FCSTD DOCUMENT  (FreeCAD 0.18R13588 (Git))
Label: footprint-template-roundrect-polylines
License: All rights reserved
LicenseURL: http://en.wikipedia.org/wiki/All_rights_reserved
objects: Sketcher::SketchObject×3, App::Annotation×2, App::DocumentObjectGroup×1
note: 3 computed .brp shape members not serialized (recipe doc carries the construction recipe); baked Part::Feature solids carry a one-line shape summary decoded from their .brp

FEATURE [App::Annotation] Text  label="Ref#_1.0mm"
  LabelText = REF**
  Position = (-30,-16,0)
FEATURE [App::Annotation] Text001  label="Value#_1.0mm"
  LabelText = Value 
  Position = (-30,-20,0)
FEATURE [Sketcher::SketchObject] Sketch003  label="F_Silks_0.16"
  sketch-geometry (4):
    g0: LineSegment StartX=-36 StartY=14 StartZ=0 EndX=24 EndY=14 EndZ=0
    g1: LineSegment StartX=24 StartY=14 StartZ=0 EndX=24 EndY=-26 EndZ=0
    g2: LineSegment StartX=24 StartY=-26 StartZ=0 EndX=-36 EndY=-26 EndZ=0
    g3: LineSegment StartX=-36 StartY=-26 StartZ=0 EndX=-36 EndY=14 EndZ=0
  constraints (12):
    c: Coincident(g0,g1)
    c: Coincident(g1,g2)
    c: Coincident(g2,g3)
    c: Coincident(g3,g0)
    c: Horizontal(g0)
    c: Horizontal(g2)
    c: Vertical(g1)
    c: Vertical(g3)
    c: DistanceY(g3,g3) = 40
    c: DistanceX(g0,g0) = 60
    c: DistanceY(g-1,g0) = 14
    c: DistanceX(g0,g-1) = 36
FEATURE [Sketcher::SketchObject] Sketch007  label="Pads_Poly"
  sketch-geometry (10):
    g0: LineSegment StartX=-20 StartY=-6 StartZ=0 EndX=-14 EndY=-1 EndZ=0
    g1: LineSegment StartX=-14 StartY=-1 StartZ=0 EndX=-10 EndY=12 EndZ=0
    g2: LineSegment StartX=-10 StartY=12 StartZ=0 EndX=21 EndY=-8 EndZ=0
    g3: LineSegment StartX=21 StartY=-8 StartZ=0 EndX=-20 EndY=-6 EndZ=0
    g4: Circle CenterX=0 CenterY=0 CenterZ=0 NormalX=0 NormalY=0 NormalZ=1 AngleXU=0 Radius=1.5
    g5: LineSegment StartX=-25 StartY=-18 StartZ=0 EndX=-21 EndY=-12 EndZ=0
    g6: LineSegment StartX=-21 StartY=-12 StartZ=0 EndX=-9 EndY=-16 EndZ=0
    g7: LineSegment StartX=-9 StartY=-16 StartZ=0 EndX=-21 EndY=-22 EndZ=0
    g8: LineSegment StartX=-21 StartY=-22 StartZ=0 EndX=-25 EndY=-18 EndZ=0
    g9: Circle CenterX=-19 CenterY=-16.5 CenterZ=0 NormalX=0 NormalY=0 NormalZ=1 AngleXU=0 Radius=1.24416
  constraints (28):
    c: Coincident(g0,g1)
    c: Coincident(g1,g2)
    c: Coincident(g2,g3)
    c: Coincident(g3,g0)
    c: DistanceX(g0,g-1) = 14
    c: DistanceY(g0,g-1) = 1
    c: DistanceX(g0,g-1) = 20
    c: DistanceY(g0,g-1) = 6
    c: DistanceX(g-1,g2) = 21
    c: DistanceY(g2,g-1) = 8
    c: DistanceX(g1,g-1) = 10
    c: DistanceY(g-1,g1) = 12
    c: Coincident(g4,g-1)
    c: Radius(g4) = 1.5
    c: Coincident(g5,g6)
    c: Coincident(g6,g7)
    c: Coincident(g7,g8)
    c: Coincident(g8,g5)
    c: DistanceX(g5,g-1) = 21
    c: DistanceY(g5,g-1) = 12
    c: DistanceX(g6) = -9
    c: DistanceY(g6,g-1) = 16
    c: DistanceX(g7,g-1) = 21
    c: DistanceY(g7,g-1) = 22
    c: DistanceX(g5,g-1) = 25
    c: DistanceY(g5,g-1) = 18
    c: DistanceY(g9,g-1) = 16.5
    c: DistanceX(g9,g-1) = 19
FEATURE [Sketcher::SketchObject] Sketch010  label="Pads_Round_Rect"
  sketch-geometry (29):
    g0: LineSegment StartX=4.5 StartY=-14 StartZ=0 EndX=11.5 EndY=-14 EndZ=0
    g1: LineSegment StartX=13 StartY=-15.5 StartZ=0 EndX=13 EndY=-18.5 EndZ=0
    g2: LineSegment StartX=11.5 StartY=-20 StartZ=0 EndX=4.5 EndY=-20 EndZ=0
    g3: LineSegment StartX=3 StartY=-18.5 StartZ=0 EndX=3 EndY=-15.5 EndZ=0
    g4: ArcOfCircle CenterX=4.5 CenterY=-15.5 CenterZ=0 NormalX=0 NormalY=0 NormalZ=1 AngleXU=0 Radius=1.5 StartAngle=1.5708 EndAngle=3.14159
    g5: ArcOfCircle CenterX=4.5 CenterY=-18.5 CenterZ=0 NormalX=0 NormalY=0 NormalZ=1 AngleXU=0 Radius=1.5 StartAngle=3.14159 EndAngle=4.71239
    g6: ArcOfCircle CenterX=11.5 CenterY=-18.5 CenterZ=0 NormalX=0 NormalY=0 NormalZ=1 AngleXU=0 Radius=1.5 StartAngle=4.71239 EndAngle=6.28319
    g7: ArcOfCircle CenterX=11.5 CenterY=-15.5 CenterZ=0 NormalX=0 NormalY=0 NormalZ=1 AngleXU=0 Radius=1.5 StartAngle=0 EndAngle=1.5708
    g8: LineSegment StartX=-23.8 StartY=9.8 StartZ=0 EndX=-22 EndY=9.8 EndZ=0
    g9: LineSegment StartX=-20.6 StartY=8.4 StartZ=0 EndX=-20.6 EndY=4.4 EndZ=0
    g10: LineSegment StartX=-22 StartY=3 StartZ=0 EndX=-23.8 EndY=3 EndZ=0
    g11: LineSegment StartX=-25.2 StartY=4.4 StartZ=0 EndX=-25.2 EndY=8.4 EndZ=0
    g12: ArcOfCircle CenterX=-23.8 CenterY=8.4 CenterZ=0 NormalX=0 NormalY=0 NormalZ=1 AngleXU=0 Radius=1.4 StartAngle=1.5708 EndAngle=3.14159
    g13: ArcOfCircle CenterX=-23.8 CenterY=4.4 CenterZ=0 NormalX=0 NormalY=0 NormalZ=1 AngleXU=0 Radius=1.4 StartAngle=3.14159 EndAngle=4.71239
    g14: ArcOfCircle CenterX=-22 CenterY=4.4 CenterZ=0 NormalX=0 NormalY=0 NormalZ=1 AngleXU=0 Radius=1.4 StartAngle=4.71239 EndAngle=6.28319
    g15: ArcOfCircle CenterX=-22 CenterY=8.4 CenterZ=0 NormalX=0 NormalY=0 NormalZ=1 AngleXU=0 Radius=1.4 StartAngle=0 EndAngle=1.5708
    g16: Circle CenterX=9.5 CenterY=-16.5 CenterZ=0 NormalX=0 NormalY=0 NormalZ=1 AngleXU=0 Radius=1.5
    g17: LineSegment StartX=13.9117 StartY=9.85944 StartZ=0 EndX=17.9117 EndY=9.85944 EndZ=0
    g18: LineSegment StartX=19.4117 StartY=8.35944 StartZ=0 EndX=19.4117 EndY=2.35944 EndZ=0
    g19: LineSegment StartX=17.9117 StartY=0.859441 StartZ=0 EndX=13.9117 EndY=0.859441 EndZ=0
    g20: LineSegment StartX=12.4117 StartY=2.35944 StartZ=0 EndX=12.4117 EndY=8.35944 EndZ=0
    g21: ArcOfCircle CenterX=13.9117 CenterY=8.35944 CenterZ=0 NormalX=0 NormalY=0 NormalZ=1 AngleXU=0 Radius=1.5 StartAngle=1.5708 EndAngle=3.14159
    g22: ArcOfCircle CenterX=13.9117 CenterY=2.35944 CenterZ=0 NormalX=0 NormalY=0 NormalZ=1 AngleXU=0 Radius=1.5 StartAngle=3.14159 EndAngle=4.71239
    g23: ArcOfCircle CenterX=17.9117 CenterY=2.35944 CenterZ=0 NormalX=0 NormalY=0 NormalZ=1 AngleXU=0 Radius=1.5 StartAngle=4.71239 EndAngle=6.28319
    g24: ArcOfCircle CenterX=17.9117 CenterY=8.35944 CenterZ=0 NormalX=0 NormalY=0 NormalZ=1 AngleXU=0 Radius=1.5 StartAngle=0 EndAngle=1.5708
    g25: ArcOfCircle CenterX=16.8103 CenterY=4.37059 CenterZ=0 NormalX=0 NormalY=0 NormalZ=1 AngleXU=0 Radius=1.0008 StartAngle=3.14159 EndAngle=6.28319
    g26: ArcOfCircle CenterX=16.8103 CenterY=6.43891 CenterZ=0 NormalX=0 NormalY=0 NormalZ=1 AngleXU=0 Radius=1.0008 StartAngle=0 EndAngle=3.14159
    g27: LineSegment StartX=17.8111 StartY=4.37059 StartZ=0 EndX=17.8111 EndY=6.43891 EndZ=0
    g28: LineSegment StartX=15.8095 StartY=4.37059 StartZ=0 EndX=15.8095 EndY=6.43891 EndZ=0
  constraints (67):
    c: Horizontal(g0)
    c: Horizontal(g2)
    c: Vertical(g1)
    c: Vertical(g3)
    c: Tangent(g0,g4) = 1.5708
    c: Tangent(g3,g4) = 1.5708
    c: Tangent(g3,g5) = 1.5708
    c: Tangent(g2,g5) = 1.5708
    c: Tangent(g1,g6) = 1.5708
    c: Tangent(g2,g6) = 1.5708
    c: Tangent(g1,g7) = 1.5708
    c: Tangent(g0,g7) = 1.5708
    c: DistanceX(g3,g1) = 10
    c: DistanceY(g2,g0) = 6
    c: Equal(g7,g4)
    c: Equal(g4,g5)
    c: Equal(g6,g5)
    c: Radius(g4) = 1.5
    c: DistanceY(g0,g-1) = 14
    c: DistanceX(g-1,g0) = 4.5
    c: Horizontal(g8)
    c: Horizontal(g10)
    c: Vertical(g9)
    c: Vertical(g11)
    c: Tangent(g8,g12) = 1.5708
    c: Tangent(g11,g12) = 1.5708
    c: Tangent(g11,g13) = 1.5708
    c: Tangent(g10,g13) = 1.5708
    c: Tangent(g9,g14) = 1.5708
    c: Tangent(g10,g14) = 1.5708
    c: Tangent(g9,g15) = 1.5708
    c: Tangent(g8,g15) = 1.5708
    c: DistanceX(g11,g9) = 4.6
    c: DistanceY(g10,g8) = 6.8
    c: Equal(g15,g12)
    c: Equal(g12,g13)
    c: Equal(g14,g13)
    c: Radius(g12) = 1.4
    c: DistanceX(g10,g-1) = 22
    c: DistanceY(g-1,g10) = 3
    c: Radius(g16) = 1.5
    c: DistanceX(g-1,g16) = 9.5
    c: DistanceY(g16,g-1) = 16.5
    c: Horizontal(g17)
    c: Horizontal(g19)
    c: Vertical(g18)
    c: Vertical(g20)
    c: Tangent(g17,g21) = 1.5708
    c: Tangent(g20,g21) = 1.5708
    c: Tangent(g20,g22) = 1.5708
    c: Tangent(g19,g22) = 1.5708
    c: Tangent(g18,g23) = 1.5708
    c: Tangent(g19,g23) = 1.5708
    c: Tangent(g18,g24) = 1.5708
    c: Tangent(g17,g24) = 1.5708
    c: DistanceX(g20,g18) = 7
    c: DistanceY(g19,g17) = 9
    c: Equal(g24,g21)
    c: Equal(g21,g22)
    c: Equal(g23,g22)
    c: Radius(g21) = 1.5
    c: Tangent(g25,g28) = 1.5708
    c: Tangent(g25,g27) = -1.5708
    c: Tangent(g27,g26) = -1.5708
    c: Tangent(g28,g26) = 1.5708
    c: Vertical(g27)
    c: Equal(g25,g26)
FEATURE [App::DocumentObjectGroup] Group  label="fp-template-roundrect-poly"
  Group = -> [Sketch003,Sketch007,Sketch010,Text,Text001]
